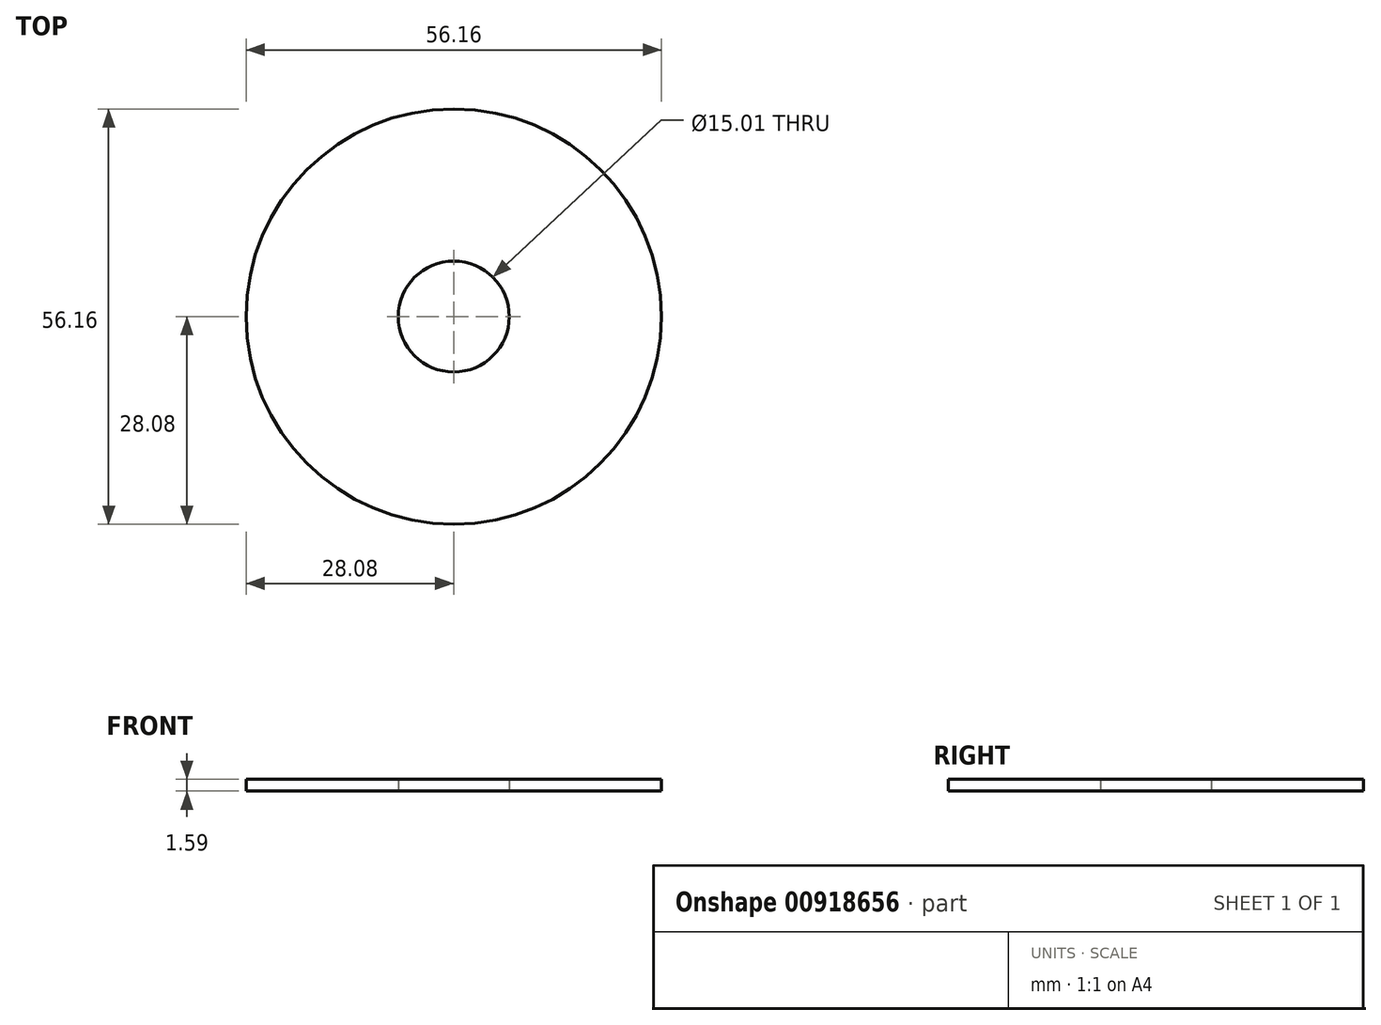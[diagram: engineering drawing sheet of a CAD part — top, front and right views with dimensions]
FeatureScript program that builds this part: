
annotation { "Feature Type Name" : "Feature", "Feature Type Description" : "" }
export const myFeature = defineFeature(function(context is Context, id is Id, definition is map)
    precondition{}
    {
        {
            var Q0;
            Q0=qCreatedBy(makeId("Top.planeOp"),FACE);
            var sketch = newSketch(context, id + "F0", { "sketchPlane" : qUnion([Q0])});
            skCircle(sketch, "E0", {"center": v(0, 0) * mm, "radius": 28.08 * mm});
            skCircle(sketch, "E1", {"center": v(0, 0) * mm, "radius": 7.5 * mm});
            skSolve(sketch);
        }
        {
            var Q0;
            Q0=makeQuery(id+"F0.imprint","IMPRINT",FACE,{"disambiguationData":[TD([[makeQuery(id+"F0.imprint","IMPRINT",EDGE,{"derivedFrom":sQuery(id+"F0.wireOp",EDGE,"E0")}),1.0]])]});
            extrude(context, id + "F1", {"entities" : qUnion([Q0]), "depth" : 1.59 * mm, "offsetDistance" : 25 * mm});
        }
    });
